# Revit family: VTp732 Тройник 90 с переходом на ВР
name_source: partatom
category: Соединительные детали трубопроводов
revit_build: Autodesk Revit 2015 (Build: 20140606_1530(x64)
units: mm (PartAtom-declared; Revit-internal decimal feet)

## types (6) — shared parameters
Группа модели = VTp.700
Изготовитель = VALTEC S.R.L.
Коэффициент K = 0.5
Метод определения потерь = Коэффициент K
Описание = Тройник 90 с переходом на внутр.резьбу
Таблица коэффициентов K = Angle Valve Threaded

## per-type parameters (varying)
| type | 20Х3/4" | 20х1/2" | 25х1/2" | 25х3/4" | 32х1" | 32х3/4" | A | B | G | Lr | d | Код по классификатору | Сц |
| 20х1/2" | Нет | Да | Нет | Нет | Нет | Нет | 51 мм | 15 мм | 15 мм | 8 мм | 20 мм | VTp.732.0.02004 | 32 мм |
| 20Х3/4" | Да | Нет | Нет | Нет | Нет | Нет | 51 мм | 15 мм | 20 мм | 8 мм | 20 мм | VTp.732.0.02005 | 34 мм |
| 25х3/4" | Нет | Нет | Нет | Да | Нет | Нет | 59 мм | 17 мм | 20 мм | 12 мм | 25 мм | VTp.732.0.02505 | 35 мм |
| 25х1/2" | Нет | Нет | Да | Нет | Нет | Нет | 59 мм | 17 мм | 15 мм | 8 мм | 25 мм | VTp.732.0.02504 | 35 мм |
| 32х3/4" | Нет | Нет | Нет | Нет | Нет | Да | 71 мм | 19 мм | 20 мм | 12 мм | 32 мм | VTp.732.0.03205 | 42 мм |
| 32х1" | Нет | Нет | Нет | Нет | Да | Нет | 71 мм | 19 мм | 25 мм | 14 мм | 32 мм | VTp.732.0.03206 | 44 мм |
